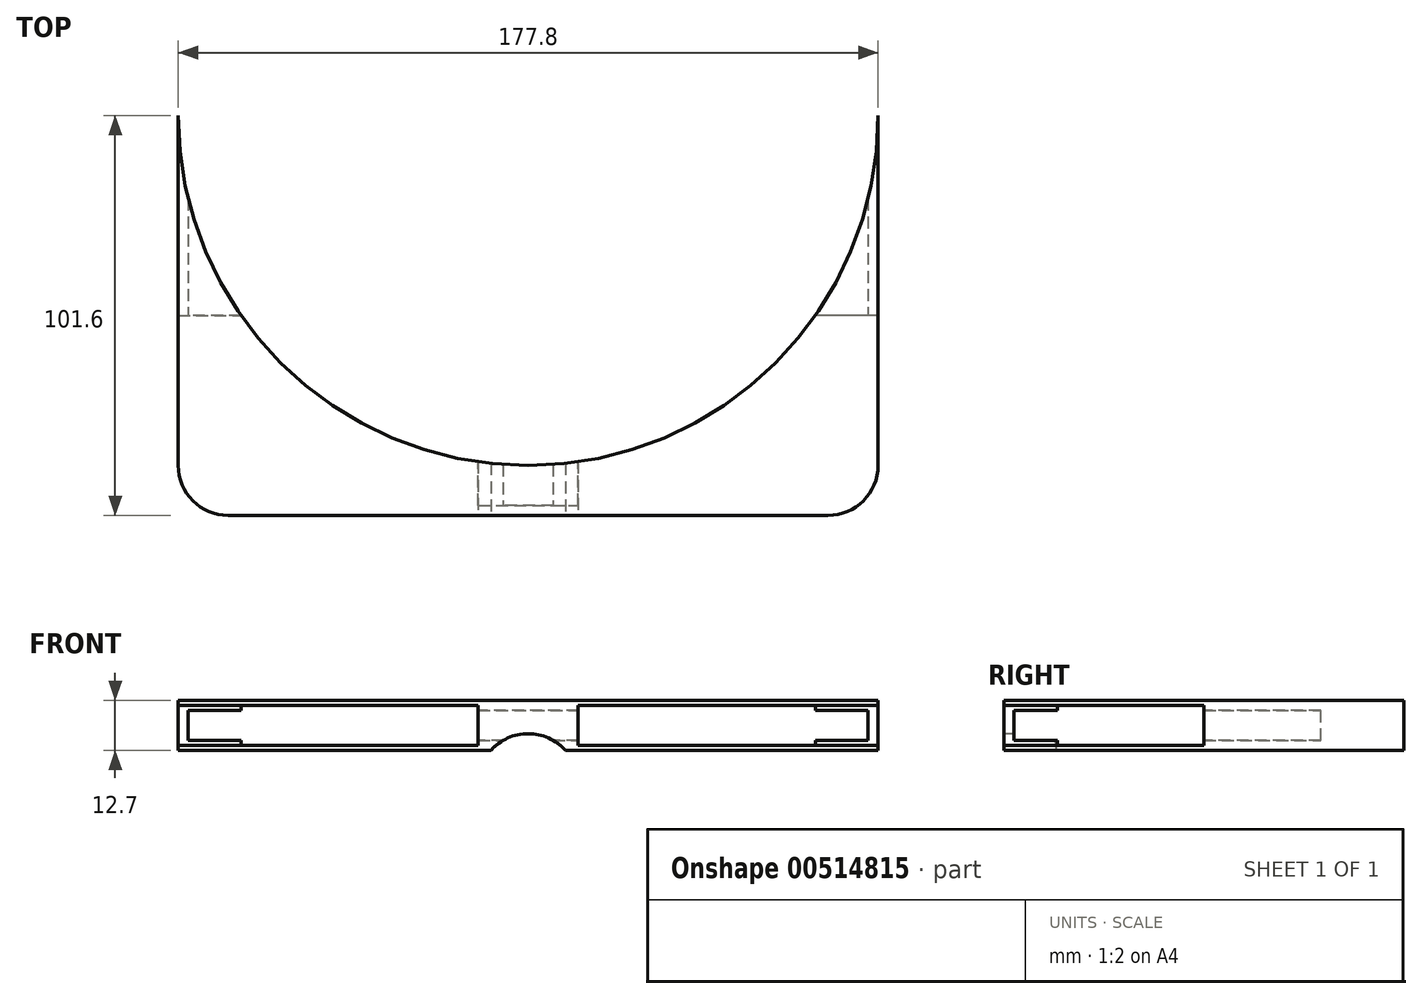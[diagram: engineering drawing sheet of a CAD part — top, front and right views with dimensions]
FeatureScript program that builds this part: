
annotation { "Feature Type Name" : "Feature", "Feature Type Description" : "" }
export const myFeature = defineFeature(function(context is Context, id is Id, definition is map)
    precondition{}
    {
        {
            var Q0;
            Q0=qCreatedBy(makeId("Front.planeOp"),FACE);
            var sketch = newSketch(context, id + "F0", { "sketchPlane" : qUnion([Q0])});
            skLineSegment(sketch, "E0.bottom", {"start": v(0, 0) * mm, "end": v(177.8, 0) * mm});
            skLineSegment(sketch, "E0.top", {"start": v(0, 12.7) * mm, "end": v(177.8, 12.7) * mm});
            skLineSegment(sketch, "E0.left", {"start": v(0, 0) * mm, "end": v(0, 12.7) * mm});
            skLineSegment(sketch, "E0.right", {"start": v(177.8, 0) * mm, "end": v(177.8, 12.7) * mm});
            skSolve(sketch);
        }
        {
            var Q0;
            Q0=makeQuery(id+"F0.imprint","IMPRINT",FACE,{"disambiguationData":[TD([[makeQuery(id+"F0.imprint","IMPRINT",EDGE,{"derivedFrom":sQuery(id+"F0.wireOp",EDGE,"E0.bottom")}),1.0]])]});
            extrude(context, id + "F1", {"entities" : qUnion([Q0]), "oppositeDirection" : true, "depth" : 101.6 * mm, "offsetDistance" : 25.4 * mm});
        }
        {
            var Q0;
            Q0=makeQuery(id+"F1.opExtrude","SWEPT_FACE",FACE,{"disambiguationData":[OSD([sQuery(id+"F0.wireOp",EDGE,"E0.top")])]});
            var sketch = newSketch(context, id + "F2", { "sketchPlane" : qUnion([Q0])});
            skCircle(sketch, "E1", {"center": v(88.9, 101.6) * mm, "radius": 88.9 * mm});
            skSolve(sketch);
        }
        {
            var Q0;
            Q0 = qSketchRegion(id + "F2", true);
            extrude(context, id + "F3", {"entities" : qUnion([Q0]), "operationType" : NewBodyOperationType.REMOVE, "oppositeDirection" : true, "depth" : 25.4 * mm, "offsetDistance" : 25.4 * mm});
        }
        {
            var Q0;
            Q0=makeQuery(id+"F3.boolean.opBoolean","COPY",FACE,{"derivedFrom":makeQuery(id+"F3.opExtrude","SWEPT_FACE",FACE,{"disambiguationData":[OSD([sQuery(id+"F2.wireOp",EDGE,"E1")])]})});
            shell(context, id + "F4", {"entities" : qUnion([Q0]), "thickness" : 2.54 * mm});
        }
        {
            var Q0;
            Q0=makeQuery(id+"F1.opExtrude","CAP_FACE",FACE,{"disambiguationData":[OSD([sQuery(id+"F0.wireOp",EDGE,"E0.bottom"),sQuery(id+"F0.wireOp",EDGE,"E0.top"),sQuery(id+"F0.wireOp",EDGE,"E0.left"),sQuery(id+"F0.wireOp",EDGE,"E0.right")])],"isStart":true});
            var sketch = newSketch(context, id + "F5", { "sketchPlane" : qUnion([Q0])});
            skLineSegment(sketch, "E2.bottom", {"start": v(0, 11.43) * mm, "end": v(76.2, 11.43) * mm});
            skLineSegment(sketch, "E2.top", {"start": v(0, 1.27) * mm, "end": v(76.2, 1.27) * mm});
            skLineSegment(sketch, "E2.left", {"start": v(0, 11.43) * mm, "end": v(0, 1.27) * mm});
            skLineSegment(sketch, "E2.right", {"start": v(76.2, 11.43) * mm, "end": v(76.2, 1.27) * mm});
            skLineSegment(sketch, "E3", {"start": v(88.9, 12.7) * mm, "end": v(88.9, 0) * mm, "construction": true});
            skLineSegment(sketch, "E4.MirrorCS", {"start": v(101.6, 11.43) * mm, "end": v(101.6, 1.27) * mm});
            skLineSegment(sketch, "E5.MirrorCS", {"start": v(177.8, 11.43) * mm, "end": v(101.6, 11.43) * mm});
            skLineSegment(sketch, "E6.MirrorCS", {"start": v(177.8, 1.27) * mm, "end": v(101.6, 1.27) * mm});
            skLineSegment(sketch, "E7.MirrorCS", {"start": v(177.8, 11.43) * mm, "end": v(177.8, 1.27) * mm});
            skSolve(sketch);
        }
        {
            var Q0;
            Q0 = qSketchRegion(id + "F5", true);
            extrude(context, id + "F6", {"entities" : qUnion([Q0]), "operationType" : NewBodyOperationType.REMOVE, "oppositeDirection" : true, "depth" : 50.8 * mm, "offsetDistance" : 25.4 * mm});
        }
        {
            var Q0;
            {var subQ0=sQuery(id+"F0.wireOp",EDGE,"E0.right");var subQ1=sQuery(id+"F0.wireOp",EDGE,"E0.top");Q0=makeQuery(id+"F6.boolean.opBoolean","SPLIT",EDGE,{"disambiguationData":[TD([makeQuery(id+"F1.opExtrude","SWEPT_FACE",FACE,{"disambiguationData":[OSD([subQ1])]})])],"derivedFrom":makeQuery(id+"F1.opExtrude","CAP_EDGE",EDGE,{"disambiguationData":[OSD([subQ0])],"isStart":true})});}
            var Q1;
            {var subQ0=sQuery(id+"F0.wireOp",EDGE,"E0.bottom");var subQ1=sQuery(id+"F0.wireOp",EDGE,"E0.right");Q1=makeQuery(id+"F6.boolean.opBoolean","SPLIT",EDGE,{"disambiguationData":[TD([makeQuery(id+"F1.opExtrude","SWEPT_FACE",FACE,{"disambiguationData":[OSD([subQ0])]})])],"derivedFrom":makeQuery(id+"F1.opExtrude","CAP_EDGE",EDGE,{"disambiguationData":[OSD([subQ1])],"isStart":true})});}
            var Q2;
            {var subQ0=sQuery(id+"F0.wireOp",EDGE,"E0.left");var subQ1=sQuery(id+"F0.wireOp",EDGE,"E0.top");Q2=makeQuery(id+"F6.boolean.opBoolean","SPLIT",EDGE,{"disambiguationData":[TD([makeQuery(id+"F1.opExtrude","SWEPT_FACE",FACE,{"disambiguationData":[OSD([subQ1])]})])],"derivedFrom":makeQuery(id+"F1.opExtrude","CAP_EDGE",EDGE,{"disambiguationData":[OSD([subQ0])],"isStart":true})});}
            var Q3;
            {var subQ0=sQuery(id+"F0.wireOp",EDGE,"E0.bottom");var subQ1=sQuery(id+"F0.wireOp",EDGE,"E0.left");Q3=makeQuery(id+"F6.boolean.opBoolean","SPLIT",EDGE,{"disambiguationData":[TD([makeQuery(id+"F1.opExtrude","SWEPT_FACE",FACE,{"disambiguationData":[OSD([subQ0])]})])],"derivedFrom":makeQuery(id+"F1.opExtrude","CAP_EDGE",EDGE,{"disambiguationData":[OSD([subQ1])],"isStart":true})});}
            fillet(context, id + "F7", {"entities" : qUnion([Q0, Q1, Q2, Q3]), "radius" : 12.7 * mm, "tangentPropagation" : true, "allowEdgeOverflow" : false});
        }
        {
            var Q0;
            Q0=makeQuery(id+"F1.opExtrude","CAP_FACE",FACE,{"disambiguationData":[OSD([sQuery(id+"F0.wireOp",EDGE,"E0.bottom"),sQuery(id+"F0.wireOp",EDGE,"E0.top"),sQuery(id+"F0.wireOp",EDGE,"E0.left"),sQuery(id+"F0.wireOp",EDGE,"E0.right")])],"isStart":true});
            var sketch = newSketch(context, id + "F8", { "sketchPlane" : qUnion([Q0])});
            skCircle(sketch, "E8", {"center": v(88.9, -8.46) * mm, "radius": 12.7 * mm});
            skSolve(sketch);
        }
        {
            var Q0;
            Q0 = qSketchRegion(id + "F8", true);
            extrude(context, id + "F9", {"entities" : qUnion([Q0]), "operationType" : NewBodyOperationType.REMOVE, "oppositeDirection" : true, "depth" : 25.4 * mm, "offsetDistance" : 25.4 * mm});
        }
    });
